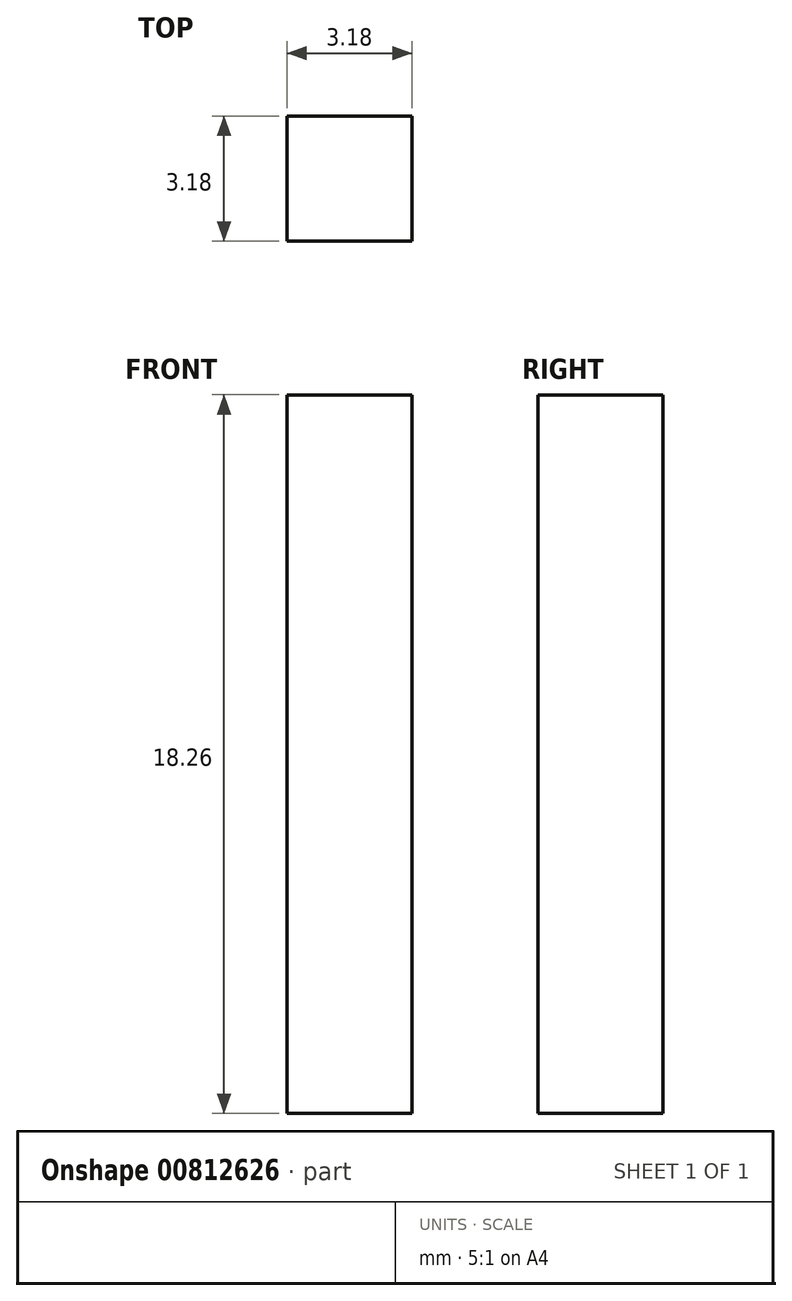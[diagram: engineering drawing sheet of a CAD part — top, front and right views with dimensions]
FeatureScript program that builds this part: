
annotation { "Feature Type Name" : "Feature", "Feature Type Description" : "" }
export const myFeature = defineFeature(function(context is Context, id is Id, definition is map)
    precondition{}
    {
        {
            var Q0;
            Q0=qCreatedBy(makeId("Top.planeOp"),FACE);
            var sketch = newSketch(context, id + "F0", { "sketchPlane" : qUnion([Q0])});
            skLineSegment(sketch, "E0.bottom", {"start": v(1.59, 1.59) * mm, "end": v(-1.59, 1.59) * mm});
            skLineSegment(sketch, "E0.top", {"start": v(1.59, -1.59) * mm, "end": v(-1.59, -1.59) * mm});
            skLineSegment(sketch, "E0.left", {"start": v(1.59, 1.59) * mm, "end": v(1.59, -1.59) * mm});
            skLineSegment(sketch, "E0.right", {"start": v(-1.59, 1.59) * mm, "end": v(-1.59, -1.59) * mm});
            skPoint(sketch, "E0.middle", {"position": v(0, 0) * mm});
            skSolve(sketch);
        }
        {
            var Q0;
            Q0 = qSketchRegion(id + "F0", true);
            extrude(context, id + "F1", {"entities" : qUnion([Q0]), "depth" : 18.26 * mm, "offsetDistance" : 25.4 * mm});
        }
    });
